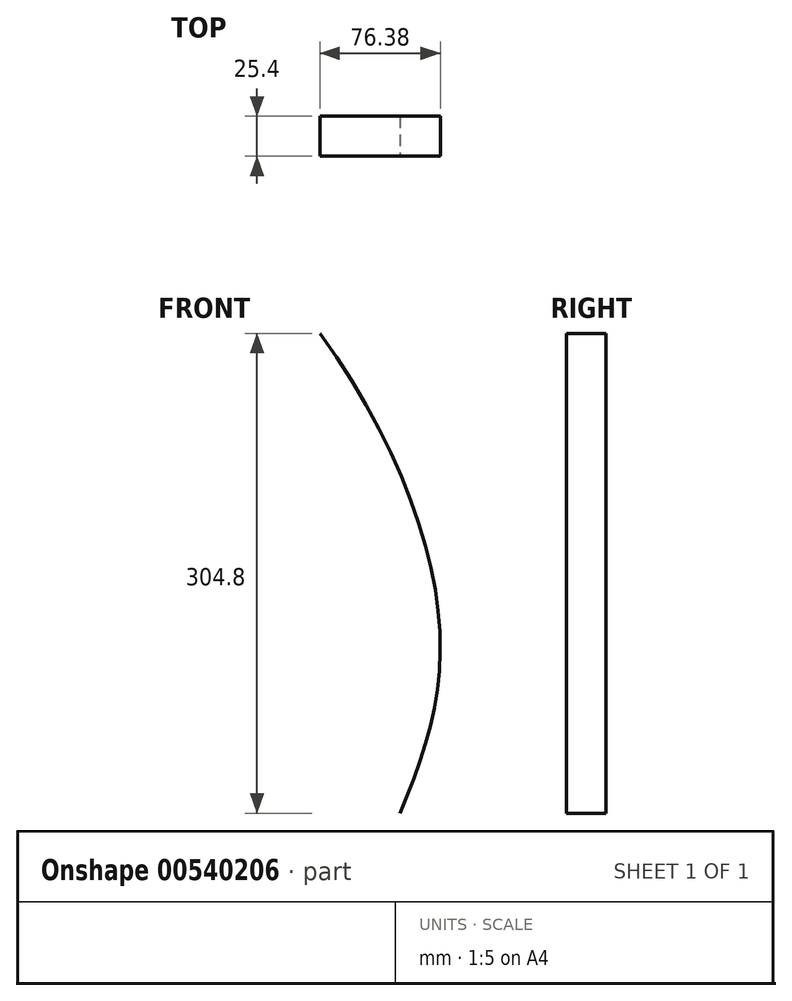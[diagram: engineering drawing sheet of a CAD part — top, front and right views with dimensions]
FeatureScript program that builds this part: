
annotation { "Feature Type Name" : "Feature", "Feature Type Description" : "" }
export const myFeature = defineFeature(function(context is Context, id is Id, definition is map)
    precondition{}
    {
        {
            var Q0;
            Q0=qCreatedBy(makeId("Front.planeOp"),FACE);
            var sketch = newSketch(context, id + "F0", { "sketchPlane" : qUnion([Q0])});
            skLineSegment(sketch, "E0", {"start": v(0, 0) * mm, "end": v(0, 304.8) * mm, "construction": true});
            skLineSegment(sketch, "E1", {"start": v(0, 304.8) * mm, "end": v(25.4, 304.8) * mm, "construction": true});
            skLineSegment(sketch, "E2", {"start": v(0, 113.82) * mm, "end": v(101.6, 113.82) * mm, "construction": true});
            skLineSegment(sketch, "E3", {"start": v(0, 0) * mm, "end": v(76.2, 0) * mm, "construction": true});
            skFitSpline(sketch, "E4", {"points": [v(76.2, 0) * mm, v(101.6, 113.82) * mm, v(25.4, 304.8) * mm], "startDerivative": vector(107.42, 256.71) * mm, "endDerivative": vector(-250.4, 348.15) * mm});
            skSolve(sketch);
        }
        {
            var Q0;
            Q0=sQuery(id+"F0.wireOp",EDGE,"E4");
            extrude(context, id + "F1", {"bodyType" : ToolBodyType.SURFACE, "surfaceEntities" : qUnion([Q0]), "depth" : 25.4 * mm, "offsetDistance" : 25.4 * mm});
        }
    });
